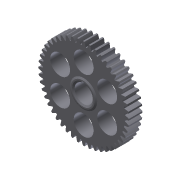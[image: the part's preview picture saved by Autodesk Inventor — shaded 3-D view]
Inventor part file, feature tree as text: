
AUTODESK INVENTOR PART (.ipt)
format: ipt  version: 2013 (Build 170138000, 138)  size: 427,520 bytes
history: native  units: mm (DEFAULTED — no unit token found)
features: sketch x6, extrude x4, plane x3, other x3, revolve x1, pattern_circular x1, projected_geometry x1
ambient origin geometry x8: Origin, YZ Plane, XZ Plane, XY Plane, X Axis, Y Axis, Z Axis, Center Point
bodies: Solid1 (feature_tree)
feature tree (19):
  extrude  "Extrusion1"  Depth=9.525mm TaperAngle=0.0deg
  plane  "Work Plane1"
  plane  "Work Plane2"
  plane  "Work Plane3"
  other  "Spur Gear"
  extrude  "Extrusion2"  Depth=76.2mm TaperAngle=0.0deg
  extrude  "Extrusion3"  Depth=19.05mm
  revolve  "Revolution1"  [1 undecoded]
  extrude  "Extrusion4"  Depth=1.143mm
  pattern_circular  "Circular Pattern1"  [2 undecoded]
  sketch  "Sketch1"  dims[d0=63.5mm d1=9.525mm d2=0.0mm]
  sketch  "Sketch2"  dims[d3=60.96mm d4=76.2mm d5=0.0mm]
  other  "Srf1"
  sketch  "Sketch3"  dims[d6=0.0mm d7=0.654498mm d20=19.05mm]
  sketch  "Sketch4"  dims[d21=0.635mm d22=0.0mm d23=12.7mm]
  sketch  "Sketch5"  dims[d24=0.635mm d25=0.0mm d26=1.143mm]
  sketch  "Sketch6"  dims[d27=0.889mm d28=5.148721mm d29=2.54mm d30=90.0deg d31=12.7mm d32=3.175mm d33=3.175mm d34=13.97mm d35=19.05mm d36=25.4mm d37=0.0mm d38=60.0mm d39=360.0deg]
  other  "Pitch Diameter"
  projected_geometry  "Project Cut Edges1"
note: 3 required parameter values undecoded (feature->parameter linkage not recoverable at this tier; creation-order binding heuristic only, values carry confidence <= 0.55)